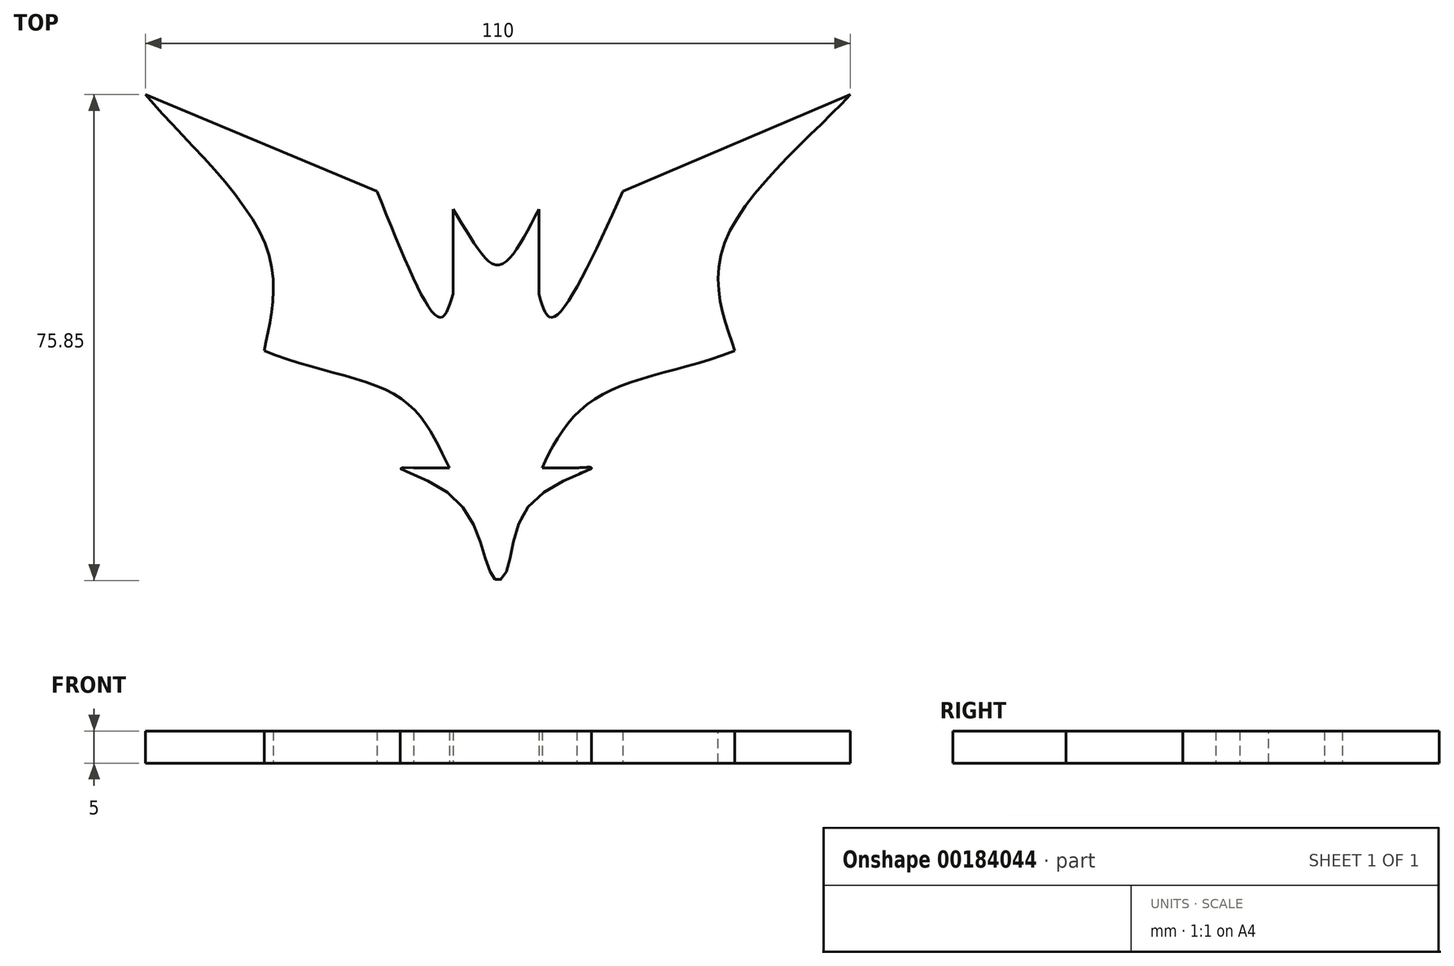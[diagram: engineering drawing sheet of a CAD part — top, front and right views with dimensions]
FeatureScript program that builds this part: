
annotation { "Feature Type Name" : "Feature", "Feature Type Description" : "" }
export const myFeature = defineFeature(function(context is Context, id is Id, definition is map)
    precondition{}
    {
        {
            var Q0;
            Q0=qCreatedBy(makeId("Top.planeOp"),FACE);
            var sketch = newSketch(context, id + "F0", { "sketchPlane" : qUnion([Q0])});
            skLineSegment(sketch, "E0.bottom", {"start": v(-53.36, 31.11) * mm, "end": v(56.64, 31.11) * mm});
            skLineSegment(sketch, "E0.top", {"start": v(-53.36, -48.89) * mm, "end": v(56.64, -48.89) * mm});
            skLineSegment(sketch, "E0.left", {"start": v(-53.36, 31.11) * mm, "end": v(-53.36, -48.89) * mm});
            skLineSegment(sketch, "E0.right", {"start": v(56.64, 31.11) * mm, "end": v(56.64, -48.89) * mm});
            skPoint(sketch, "E1.1.internal.snap0", {"position": v(1.64, -8.89) * mm});
            skFitSpline(sketch, "E2", {"points": [v(-5.37, 13.22) * mm, v(1.64, 4.51) * mm, v(8.02, 13.22) * mm], "startDerivative": vector(16.45, -25.97) * mm, "endDerivative": vector(13.74, 26.25) * mm});
            skLineSegment(sketch, "E3", {"start": v(-5.37, 13.22) * mm, "end": v(-5.37, 0) * mm});
            skLineSegment(sketch, "E4", {"start": v(8.02, 13.22) * mm, "end": v(8.02, 0) * mm});
            skFitSpline(sketch, "E5", {"points": [v(8.02, 0) * mm, v(10, -3.7) * mm, v(21.16, 16) * mm], "startDerivative": vector(5.14, -18.37) * mm, "endDerivative": vector(19.26, 42.32) * mm});
            skFitSpline(sketch, "E6", {"points": [v(-5.37, 0) * mm, v(-7.34, -3.7) * mm, v(-17.2, 16) * mm], "startDerivative": vector(-5.33, -18.3) * mm, "endDerivative": vector(-16.81, 42.38) * mm});
            skLineSegment(sketch, "E7", {"start": v(-17.2, 16) * mm, "end": v(-53.36, 31.11) * mm});
            skLineSegment(sketch, "E8", {"start": v(21.16, 16) * mm, "end": v(56.64, 31.11) * mm});
            skFitSpline(sketch, "E9", {"points": [v(-53.36, 31.11) * mm, v(-34.48, 7.3) * mm, v(-34.8, -8.89) * mm], "startDerivative": vector(26.8, -32.44) * mm, "endDerivative": vector(-5.58, -31.05) * mm});
            skFitSpline(sketch, "E10", {"points": [v(56.64, 31.11) * mm, v(36.78, 7.3) * mm, v(38.58, -8.89) * mm], "startDerivative": vector(-29.56, -32.29) * mm, "endDerivative": vector(9.92, -31.21) * mm});
            skFitSpline(sketch, "E11", {"points": [v(-34.8, -8.89) * mm, v(-13.29, -16.46) * mm, v(-5.91, -27.17) * mm], "startDerivative": vector(40.75, -17.07) * mm, "endDerivative": vector(13.33, -25.87) * mm});
            skFitSpline(sketch, "E12", {"points": [v(38.58, -8.89) * mm, v(16.67, -16.46) * mm, v(8.54, -27.17) * mm], "startDerivative": vector(-42.88, -16.58) * mm, "endDerivative": vector(-11.95, -26.46) * mm});
            skLineSegment(sketch, "E13", {"start": v(-5.91, -27.17) * mm, "end": v(-11.5, -27.17) * mm});
            skLineSegment(sketch, "E14", {"start": v(8.54, -27.17) * mm, "end": v(13.96, -27.17) * mm});
            skFitSpline(sketch, "E15", {"points": [v(-11.5, -27.17) * mm, v(-13.63, -27.17) * mm, v(-5.09, -31.93) * mm, v(0, -42.28) * mm, v(1.64, -44.74) * mm, v(3.28, -42.44) * mm, v(7.06, -32.43) * mm, v(16.25, -27.17) * mm, v(13.96, -27.17) * mm], "startDerivative": vector(-41.84, 2.8) * mm, "endDerivative": vector(-43.97, -3.06) * mm});
            skPoint(sketch, "E16.end.orphan", {"position": v(1.64, -48.89) * mm});
            skPoint(sketch, "E17.orphan", {"position": v(1.64, 31.11) * mm});
            skSolve(sketch);
        }
        {
            var Q0;
            Q0=makeQuery(id+"F0.imprint","IMPRINT",FACE,{"disambiguationData":[TD([[makeQuery(id+"F0.imprint","IMPRINT",EDGE,{"derivedFrom":sQuery(id+"F0.wireOp",EDGE,"E2")}),-1.0]])]});
            extrude(context, id + "F1", {"entities" : qUnion([Q0]), "depth" : 5 * mm});
        }
    });
